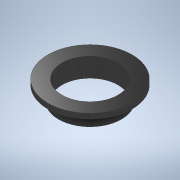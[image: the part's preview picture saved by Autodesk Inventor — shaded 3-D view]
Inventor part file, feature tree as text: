
AUTODESK INVENTOR PART (.ipt)
format: ipt  version: 2020 (Build 240168000, 168)  size: 124,416 bytes
history: native  units: in
note: dims shown in document units (in); Inventor stores cm internally (conversion verified against a paired STEP export)
features: sketch x3, extrude x2, revolve x1
ambient origin geometry x8: Origin, YZ Plane, XZ Plane, XY Plane, X Axis, Y Axis, Z Axis, Center Point
bodies: Solid1 (feature_tree)
feature tree (6):
  revolve  "Revolution1"  [1 undecoded]
  extrude  "Extrusion1"  Depth=0.25in
  extrude  "Extrusion2"  Depth=0.25in
  sketch  "Sketch1"  dims[d2=0.75in d3=0.093in]
  sketch  "Sketch2"  dims[d4=0.167in d5=0.25in]
  sketch  "Sketch3"  dims[d6=90.0deg d7=1.0in d8=1.0in d9=0.0in d10=1.125in d11=0.25in d12=0.0in]
note: 1 required parameter value undecoded (feature->parameter linkage not recoverable at this tier; creation-order binding heuristic only, values carry confidence <= 0.55)
